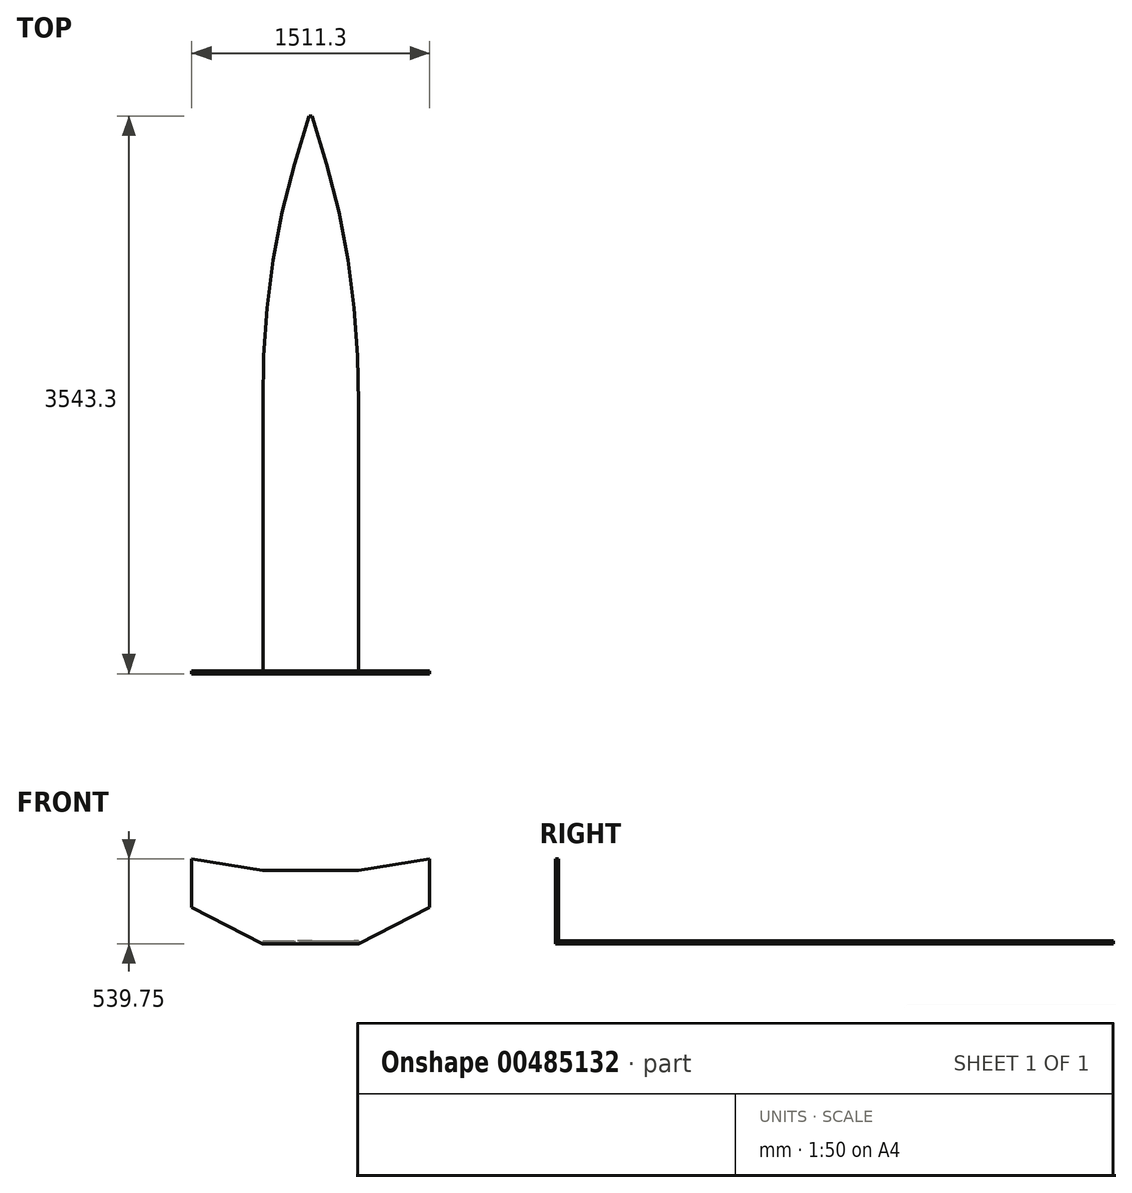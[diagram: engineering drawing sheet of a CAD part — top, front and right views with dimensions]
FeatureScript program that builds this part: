
annotation { "Feature Type Name" : "Feature", "Feature Type Description" : "" }
export const myFeature = defineFeature(function(context is Context, id is Id, definition is map)
    precondition{}
    {
        {
            var Q0;
            Q0=qCreatedBy(makeId("Front.planeOp"),FACE);
            var sketch = newSketch(context, id + "F0", { "sketchPlane" : qUnion([Q0])});
            skLineSegment(sketch, "E0", {"start": v(0, 0) * mm, "end": v(304.8, 0) * mm});
            skLineSegment(sketch, "E1", {"start": v(-304.8, 0) * mm, "end": v(0, 0) * mm});
            skLineSegment(sketch, "E2", {"start": v(0, 231.78) * mm, "end": v(-755.65, 231.77) * mm});
            skLineSegment(sketch, "E3", {"start": v(-755.65, 231.77) * mm, "end": v(-304.8, 0) * mm});
            skLineSegment(sketch, "E4", {"start": v(-755.65, 539.75) * mm, "end": v(-755.65, 231.77) * mm});
            skLineSegment(sketch, "E5", {"start": v(755.65, 539.75) * mm, "end": v(755.65, 231.78) * mm});
            skLineSegment(sketch, "E6", {"start": v(755.65, 231.78) * mm, "end": v(304.8, 0) * mm});
            skLineSegment(sketch, "E7", {"start": v(0, 231.77) * mm, "end": v(755.65, 231.78) * mm});
            skPoint(sketch, "E8.orphan", {"position": v(755.65, 539.75) * mm});
            skLineSegment(sketch, "E9", {"start": v(0, 466.72) * mm, "end": v(0, 231.77) * mm});
            skLineSegment(sketch, "E10", {"start": v(-304.8, 0) * mm, "end": v(-304.8, 466.72) * mm});
            skLineSegment(sketch, "E11", {"start": v(304.8, 0) * mm, "end": v(304.8, 466.73) * mm});
            skLineSegment(sketch, "E12", {"start": v(-304.8, 466.72) * mm, "end": v(304.8, 466.73) * mm});
            skLineSegment(sketch, "E13", {"start": v(304.8, 466.73) * mm, "end": v(755.65, 539.75) * mm});
            skLineSegment(sketch, "E14", {"start": v(-304.8, 466.73) * mm, "end": v(-755.65, 539.75) * mm});
            skSolve(sketch);
        }
        {
            var Q0;
            Q0=qCreatedBy(makeId("Top.planeOp"),FACE);
            var sketch = newSketch(context, id + "F1", { "sketchPlane" : qUnion([Q0])});
            skLineSegment(sketch, "E15", {"start": v(0, 0) * mm, "end": v(0, 171.45) * mm});
            skLineSegment(sketch, "E16", {"start": v(0, 171.45) * mm, "end": v(0, 476.25) * mm});
            skLineSegment(sketch, "E17", {"start": v(0, 476.25) * mm, "end": v(0, 781.05) * mm});
            skLineSegment(sketch, "E18", {"start": v(0, 781.05) * mm, "end": v(0, 1085.85) * mm});
            skLineSegment(sketch, "E19", {"start": v(0, 1085.85) * mm, "end": v(0, 1390.65) * mm});
            skLineSegment(sketch, "E20", {"start": v(0, 1390.65) * mm, "end": v(0, 1695.45) * mm});
            skLineSegment(sketch, "E21", {"start": v(0, 1695.45) * mm, "end": v(0, 2000.25) * mm});
            skLineSegment(sketch, "E22", {"start": v(-304.65, 171.45) * mm, "end": v(-304.65, 0) * mm});
            skLineSegment(sketch, "E23", {"start": v(302.98, 0) * mm, "end": v(302.98, 171.45) * mm});
            skLineSegment(sketch, "E24", {"start": v(-304.65, 171.45) * mm, "end": v(-304.65, 1701.35) * mm});
            skLineSegment(sketch, "E25", {"start": v(302.98, 171.45) * mm, "end": v(302.98, 1701.35) * mm});
            skLineSegment(sketch, "E26", {"start": v(0, 2000.25) * mm, "end": v(-298.45, 2000.25) * mm});
            skLineSegment(sketch, "E27", {"start": v(0, 2000.25) * mm, "end": v(298.45, 2000.25) * mm});
            skLineSegment(sketch, "E28", {"start": v(-304.65, 1701.35) * mm, "end": v(-298.45, 2000.25) * mm});
            skLineSegment(sketch, "E29", {"start": v(302.98, 1701.35) * mm, "end": v(298.45, 2000.25) * mm});
            skLineSegment(sketch, "E30", {"start": v(0, 2000.25) * mm, "end": v(0, 2305.05) * mm});
            skLineSegment(sketch, "E31", {"start": v(0, 2305.05) * mm, "end": v(0, 2609.85) * mm});
            skLineSegment(sketch, "E32", {"start": v(0, 2609.85) * mm, "end": v(0, 2914.65) * mm});
            skLineSegment(sketch, "E33", {"start": v(0, 2305.05) * mm, "end": v(-276.23, 2305.05) * mm});
            skLineSegment(sketch, "E34", {"start": v(0, 2305.05) * mm, "end": v(276.23, 2305.05) * mm});
            skLineSegment(sketch, "E35", {"start": v(0, 2609.85) * mm, "end": v(-238.13, 2609.85) * mm});
            skLineSegment(sketch, "E36", {"start": v(-298.45, 2000.25) * mm, "end": v(-276.23, 2305.05) * mm});
            skLineSegment(sketch, "E37", {"start": v(-276.23, 2305.05) * mm, "end": v(-238.13, 2609.85) * mm});
            skLineSegment(sketch, "E38", {"start": v(0, 2914.65) * mm, "end": v(-180.98, 2914.65) * mm});
            skLineSegment(sketch, "E39", {"start": v(-238.13, 2609.85) * mm, "end": v(-180.97, 2914.65) * mm});
            skLineSegment(sketch, "E40", {"start": v(298.45, 2000.25) * mm, "end": v(276.23, 2305.05) * mm});
            skLineSegment(sketch, "E41", {"start": v(0, 2609.85) * mm, "end": v(238.13, 2609.85) * mm});
            skLineSegment(sketch, "E42", {"start": v(238.13, 2609.85) * mm, "end": v(276.23, 2305.05) * mm});
            skLineSegment(sketch, "E43", {"start": v(0, 2914.65) * mm, "end": v(180.98, 2914.65) * mm});
            skLineSegment(sketch, "E44", {"start": v(180.97, 2914.65) * mm, "end": v(238.13, 2609.85) * mm});
            skLineSegment(sketch, "E45", {"start": v(0, 2914.65) * mm, "end": v(0, 3219.45) * mm});
            skLineSegment(sketch, "E46", {"start": v(0, 3219.45) * mm, "end": v(-101.6, 3219.45) * mm});
            skLineSegment(sketch, "E47", {"start": v(-180.97, 2914.65) * mm, "end": v(-101.6, 3219.45) * mm});
            skLineSegment(sketch, "E48", {"start": v(0, 3219.45) * mm, "end": v(101.6, 3219.45) * mm});
            skLineSegment(sketch, "E49", {"start": v(101.6, 3219.45) * mm, "end": v(180.97, 2914.65) * mm});
            skLineSegment(sketch, "E50", {"start": v(0, 3219.45) * mm, "end": v(0, 3524.25) * mm});
            skLineSegment(sketch, "E51", {"start": v(0, 3524.25) * mm, "end": v(-9.53, 3524.25) * mm});
            skLineSegment(sketch, "E52", {"start": v(0, 3524.25) * mm, "end": v(9.53, 3524.25) * mm});
            skLineSegment(sketch, "E53", {"start": v(-9.53, 3524.25) * mm, "end": v(-101.6, 3219.45) * mm});
            skLineSegment(sketch, "E54", {"start": v(9.53, 3524.25) * mm, "end": v(101.6, 3219.45) * mm});
            skLineSegment(sketch, "E55", {"start": v(0, 171.45) * mm, "end": v(302.98, 171.45) * mm});
            skLineSegment(sketch, "E56", {"start": v(0, 171.45) * mm, "end": v(-304.65, 171.45) * mm});
            skLineSegment(sketch, "E57", {"start": v(-304.65, 0) * mm, "end": v(302.98, 0) * mm});
            skSolve(sketch);
        }
        {
            var Q0;
            Q0 = qSketchRegion(id + "F0", true);
            extrude(context, id + "F2", {"entities" : qUnion([Q0]), "depth" : 19.05 * mm});
        }
        {
            var Q0;
            Q0 = qSketchRegion(id + "F1", true);
            extrude(context, id + "F3", {"entities" : qUnion([Q0]), "operationType" : NewBodyOperationType.ADD, "depth" : 19.05 * mm});
        }
    });
